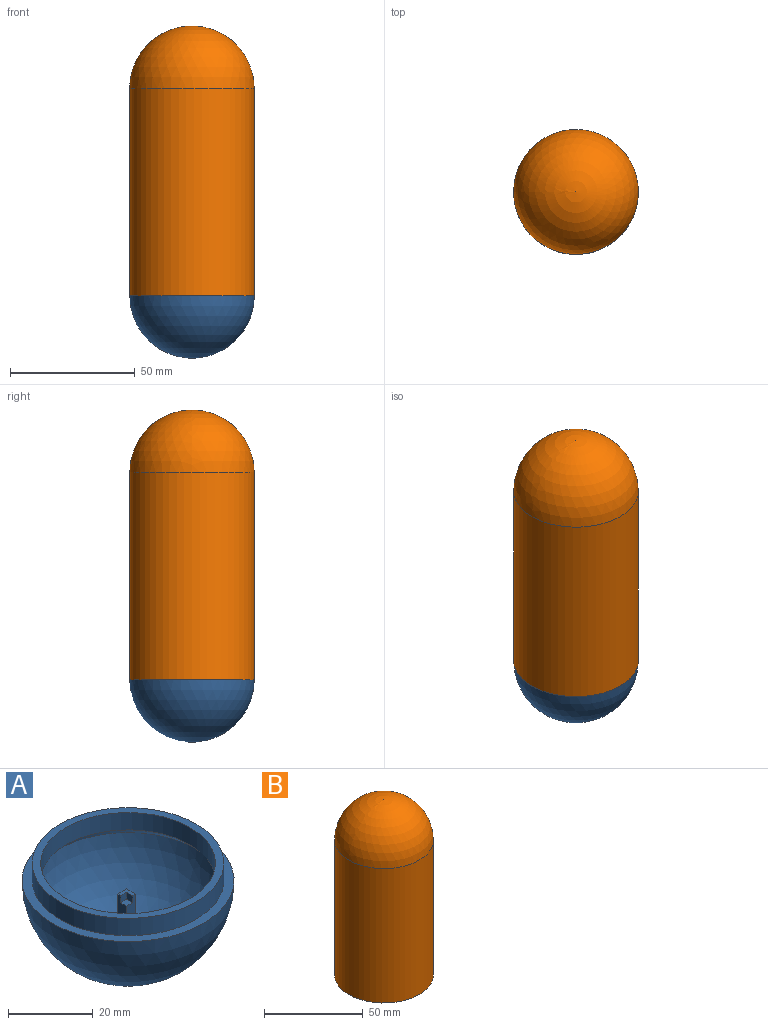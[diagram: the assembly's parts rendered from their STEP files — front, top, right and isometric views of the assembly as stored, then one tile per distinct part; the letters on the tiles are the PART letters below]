
ASSEMBLY  parts=2 mates=1
PART A: 42 faces, bbox 50x50x30 mm
  f0: sphere r=23mm, area 2901.7mm2, adj f2,f3,f10,f11,f12,f13,f14,f15
  f1: cylinder r=20.6mm len=41.2mm, axis (0,0,1), area 647.2mm2, adj f2,f9
  f2: cone r=20.6mm half-angle=44.1deg, axis (0,0,-1), area 447.4mm2, adj f0,f1
  f3: cylinder r=3.5mm len=7mm, axis (0,0,1), area 105.1mm2, adj f0,f4
  f4: plane 7x7mm, normal (0,0,1), area 31.4mm2, adj f3,f5
  f5: cylinder r=1.5mm len=7mm, axis (0,0,1), area 66mm2, adj f4,f6
  f6: sphere r=25mm, area 3919.9mm2, adj f5,f7
  f7: plane 50x50mm, normal (0,0,1), area 358.9mm2, adj f6,f8
  f8: cylinder r=22.6mm len=45.2mm, axis (0,0,1), area 710mm2, adj f7,f9
  f9: plane 45.2x45.2mm, normal (0,0,1), area 271.4mm2, adj f1,f8
  f10: plane 7.45x3mm, normal (-1,0,0), area 16.4mm2, adj f0,f11,f13,f29,f31,f39
  f11: plane 7.45x3mm, normal (0,-1,0), area 16.5mm2, adj f0,f10,f12,f30,f31,f39
  f12: plane 6.12x3mm, normal (1,0,0), area 16.3mm2, adj f0,f11,f13,f31
  f13: plane 6.05x3mm, normal (0,1,0), area 16.1mm2, adj f0,f10,f12,f31
  f14: plane 7.45x3mm, normal (0,-1,0), area 16.5mm2, adj f0,f15,f17,f26,f28,f38
  f15: plane 7.45x3mm, normal (1,0,0), area 16.4mm2, adj f0,f14,f16,f27,f28,f38
  f16: plane 6.05x3mm, normal (0,1,0), area 16.1mm2, adj f0,f15,f17,f28
  f17: plane 6.12x3mm, normal (-1,0,0), area 16.3mm2, adj f0,f14,f16,f28
  f18: plane 7.45x3mm, normal (0,1,0), area 16.5mm2, adj f0,f19,f21,f36,f37,f41
  f19: plane 6.12x3mm, normal (-1,0,0), area 16.3mm2, adj f0,f18,f20,f37
  f20: plane 6.05x3mm, normal (0,-1,0), area 16.1mm2, adj f0,f19,f21,f37
  f21: plane 7.45x3mm, normal (1,0,0), area 16.4mm2, adj f0,f18,f20,f35,f37,f41
  f22: plane 7.45x3mm, normal (-1,0,0), area 16.4mm2, adj f0,f23,f25,f33,f34,f40
  f23: plane 6.05x3mm, normal (0,-1,0), area 16.1mm2, adj f0,f22,f24,f34
  f24: plane 6.12x3mm, normal (1,0,0), area 16.3mm2, adj f0,f23,f25,f34
  f25: plane 7.45x3mm, normal (0,1,0), area 16.5mm2, adj f0,f22,f24,f32,f34,f40
  f26: plane 2x2mm, normal (1,0,0), area 4mm2, adj f14,f27,f28,f38
  f27: plane 2x2mm, normal (0,-1,0), area 4mm2, adj f15,f26,f28,f38
  f28: plane 3x3mm, normal (0,0,1), area 5mm2, adj f14,f15,f16,f17,f26,f27
  f29: plane 2x2mm, normal (0,-1,0), area 4mm2, adj f10,f30,f31,f39
  f30: plane 2x2mm, normal (-1,0,0), area 4mm2, adj f11,f29,f31,f39
  f31: plane 3x3mm, normal (0,0,1), area 5mm2, adj f10,f11,f12,f13,f29,f30
  f32: plane 2x2mm, normal (-1,0,0), area 4mm2, adj f25,f33,f34,f40
  f33: plane 2x2mm, normal (0,1,0), area 4mm2, adj f22,f32,f34,f40
  f34: plane 3x3mm, normal (0,0,1), area 5mm2, adj f22,f23,f24,f25,f32,f33
  f35: plane 2x2mm, normal (0,1,0), area 4mm2, adj f21,f36,f37,f41
  f36: plane 2x2mm, normal (1,0,0), area 4mm2, adj f18,f35,f37,f41
  f37: plane 3x3mm, normal (0,0,1), area 5mm2, adj f18,f19,f20,f21,f35,f36
  f38: plane 2x2mm, normal (0,0,1), area 4mm2, adj f14,f15,f26,f27
  f39: plane 2x2mm, normal (0,0,1), area 4mm2, adj f10,f11,f29,f30
  f40: plane 2x2mm, normal (0,0,1), area 4mm2, adj f22,f25,f32,f33
  f41: plane 2x2mm, normal (0,0,1), area 4mm2, adj f18,f21,f35,f36
PART B: 5 faces, bbox 50x50x108.3 mm
  f0: sphere r=25mm, area 3927mm2, adj f4
  f1: sphere r=23mm, area 3323.8mm2, adj f2
  f2: cylinder r=23mm len=83.3mm, axis (0,0,-1), area 12038mm2, adj f1,f3
  f3: plane 50x50mm, normal (0,0,-1), area 301.6mm2, adj f2,f4
  f4: cylinder r=25mm len=83.3mm, axis (0,0,-1), area 13084.7mm2, adj f0,f3
PLACE A t=(-1.48,0,62.37)mm
PLACE B t=(-1.48,0,53.51)mm
MATE fastened A.f1 <-> B.f2  axis (0,0,1) through (-1.48,0,87.32)mm
